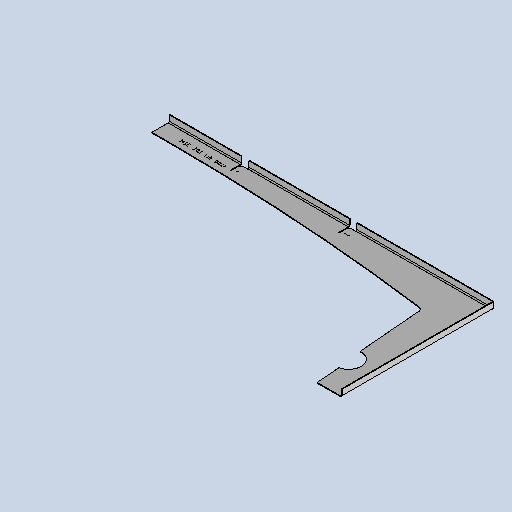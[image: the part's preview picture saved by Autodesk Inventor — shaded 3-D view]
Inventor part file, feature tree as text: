
AUTODESK INVENTOR PART (.ipt)
format: ipt  version: 2025 (Build 290162010, 162A)  size: 352,256 bytes
history: native  units: mm
features: other x6, sheet_metal_op x4, sketch x4, extrude x1
ambient origin geometry x8: Origin, YZ Plane, XZ Plane, XY Plane, X Axis, Y Axis, Z Axis, Center Point
bodies: Solid1 (feature_tree)
feature tree (15):
  sheet_metal_op  "Face1"
  other  "Mark3"
  sheet_metal_op  "Flange1"
  extrude  "Extrusion3"  Depth=2.0mm
  other  "Corner Chamfer2"
  other  "A-Side Definition"
  sketch  "Sketch1"  dims[d3=40.0mm d5=2.0mm]
  other  "Plate1"
  sketch  "Sketch2"  dims[d25=6.0mm d27=3.0mm d31=3.0mm]
  other  "Plate2"
  sheet_metal_op  "Bend1"
  sheet_metal_op  "Corner1"
  sketch  "Sketch7"  dims[d37=2.0mm]
  sketch  "Sketch8"  dims[d38=1.0mm d39=4.0mm d40=2.75mm d41=20.0mm d42=90.0deg d43=2.75mm d44=8.0mm d45=0.5mm d46=2.75mm d52=31.0mm d53=50.0mm d57=32.0mm d66=67.869053mm d76=51.965032mm d90=1500.0mm d92=2100.0mm d93=8.0mm d94=50.0mm d95=50.0mm d96=3.0mm d97=10.0mm d102=3.0mm d104=5.0mm d105=70.0mm d135=20.0mm d136=12.0mm d137=12.0mm d138=150.0mm d139=300.0mm d140=2.1mm d141=21.0mm d142=21.0mm d143=300.0mm d144=31.0mm d146=30.0mm d147=2.0mm d148=20.0mm d150=5.0mm d151=0.0mm d152=0.0mm d156=150.0mm d157=6.0mm d158=6.0mm d159=45.0deg d160=67.948864mm d161=51.991501mm d162=4.0mm d164=50.0mm d165=222.0mm d166=16.545721mm d167=900.0mm]
  other  "Definition1"
